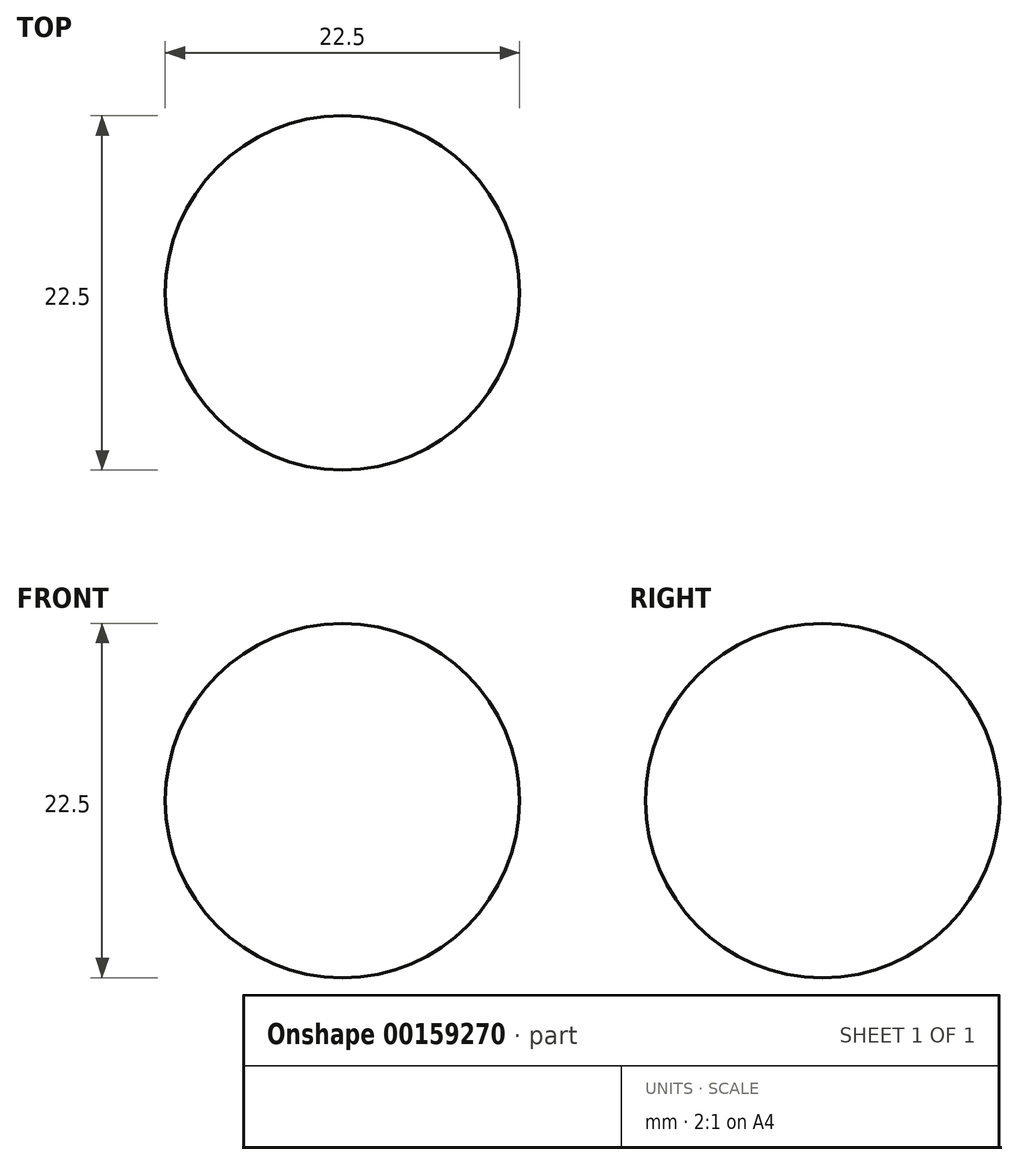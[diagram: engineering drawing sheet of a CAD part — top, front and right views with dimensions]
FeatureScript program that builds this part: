
annotation { "Feature Type Name" : "Feature", "Feature Type Description" : "" }
export const myFeature = defineFeature(function(context is Context, id is Id, definition is map)
    precondition{}
    {
        {
            var Q0;
            Q0=qCreatedBy(makeId("Right.planeOp"),FACE);
            var sketch = newSketch(context, id + "F0", { "sketchPlane" : qUnion([Q0])});
            skArc(sketch, "E0", {"start": v(0, 11.25) * mm, "mid": v(-11.25, 0) * mm, "end": v(0, -11.25) * mm});
            skLineSegment(sketch, "E1", {"start": v(0, 11.25) * mm, "end": v(0, -11.25) * mm});
            skSolve(sketch);
        }
        {
            var Q0;
            Q0=qCreatedBy(makeId("Top.planeOp"),FACE);
            var sketch = newSketch(context, id + "F1", { "sketchPlane" : qUnion([Q0])});
            skCircle(sketch, "E2", {"center": v(0, 0) * mm, "radius": 11.12 * mm});
            skSolve(sketch);
        }
        {
            var Q0;
            Q0=makeQuery(id+"F0.imprint","IMPRINT",FACE,{"disambiguationData":[TD([[makeQuery(id+"F0.imprint","IMPRINT",EDGE,{"derivedFrom":sQuery(id+"F0.wireOp",EDGE,"E0")}),1.0]])]});
            var Q1;
            Q1=sQuery(id+"F1.wireOp",EDGE,"E2");
            sweep(context, id + "F2", {"profiles" : qUnion([Q0]), "path" : qUnion([Q1])});
        }
    });
